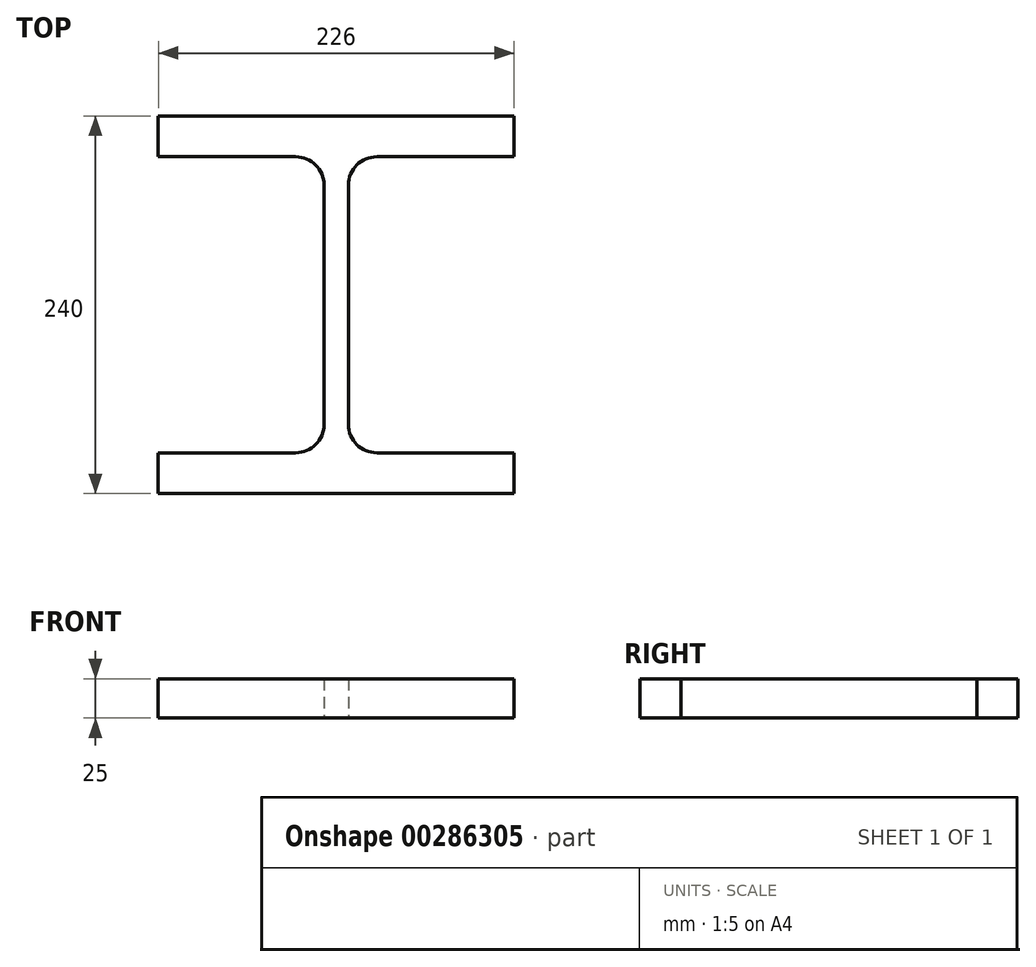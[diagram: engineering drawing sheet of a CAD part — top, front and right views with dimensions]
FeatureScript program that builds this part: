
annotation { "Feature Type Name" : "Feature", "Feature Type Description" : "" }
export const myFeature = defineFeature(function(context is Context, id is Id, definition is map)
    precondition{}
    {
        {
            var Q0;
            Q0=qCreatedBy(makeId("Top.planeOp"),FACE);
            var sketch = newSketch(context, id + "F0", { "sketchPlane" : qUnion([Q0])});
            skLineSegment(sketch, "E0", {"start": v(-45.16, 76.87) * mm, "end": v(180.84, 76.87) * mm});
            skLineSegment(sketch, "E1", {"start": v(-45.16, -163.13) * mm, "end": v(180.84, -163.13) * mm});
            skPoint(sketch, "E2.end.orphan", {"position": v(-45.16, -155.6) * mm});
            skLineSegment(sketch, "E3", {"start": v(-45.16, 76.87) * mm, "end": v(-45.16, 50.87) * mm});
            skLineSegment(sketch, "E4", {"start": v(-45.16, -163.13) * mm, "end": v(-45.16, -137.13) * mm});
            skLineSegment(sketch, "E5", {"start": v(180.84, -163.13) * mm, "end": v(180.84, -137.13) * mm});
            skLineSegment(sketch, "E6", {"start": v(180.84, 76.87) * mm, "end": v(180.84, 50.87) * mm});
            skLineSegment(sketch, "E7", {"start": v(180.84, 50.87) * mm, "end": v(93.59, 50.87) * mm});
            skLineSegment(sketch, "E8", {"start": v(60.09, -54.42) * mm, "end": v(60.09, -119.13) * mm});
            skLineSegment(sketch, "E9", {"start": v(60.09, 32.87) * mm, "end": v(60.09, -54.42) * mm});
            skLineSegment(sketch, "E10", {"start": v(75.59, -54.42) * mm, "end": v(75.59, 32.87) * mm});
            skLineSegment(sketch, "E11", {"start": v(75.59, -54.42) * mm, "end": v(75.59, -119.13) * mm});
            skLineSegment(sketch, "E12", {"start": v(-45.16, -137.13) * mm, "end": v(42.09, -137.13) * mm});
            skLineSegment(sketch, "E13", {"start": v(-45.16, 50.87) * mm, "end": v(42.09, 50.87) * mm});
            skPoint(sketch, "E14.end.orphan", {"position": v(67.84, -160.03) * mm});
            skPoint(sketch, "E15.orphan", {"position": v(54.84, 50.87) * mm});
            skPoint(sketch, "E16.visualSharp", {"position": v(60.09, 50.87) * mm});
            skArc(sketch, "E16.filletArc", {"start": v(60.09, 32.87) * mm, "mid": v(54.81, 45.6) * mm, "end": v(42.09, 50.87) * mm});
            skPoint(sketch, "E17.visualSharp", {"position": v(75.59, 50.87) * mm});
            skArc(sketch, "E17.filletArc", {"start": v(93.59, 50.87) * mm, "mid": v(80.86, 45.6) * mm, "end": v(75.59, 32.87) * mm});
            skPoint(sketch, "E18.orphan", {"position": v(75.59, -160.03) * mm});
            skPoint(sketch, "E19.orphan", {"position": v(60.09, -160.03) * mm});
            skLineSegment(sketch, "E20", {"start": v(93.59, -137.13) * mm, "end": v(180.84, -137.13) * mm});
            skPoint(sketch, "E21.visualSharp", {"position": v(60.09, -137.13) * mm});
            skArc(sketch, "E21.filletArc", {"start": v(42.09, -137.13) * mm, "mid": v(54.81, -131.86) * mm, "end": v(60.09, -119.13) * mm});
            skPoint(sketch, "E22.visualSharp", {"position": v(75.59, -137.13) * mm});
            skArc(sketch, "E22.filletArc", {"start": v(75.59, -119.13) * mm, "mid": v(80.86, -131.86) * mm, "end": v(93.59, -137.13) * mm});
            skPoint(sketch, "E23.start.orphan", {"position": v(180.84, -150.13) * mm});
            skSolve(sketch);
        }
        {
            var Q0;
            Q0=makeQuery(id+"F0.imprint","IMPRINT",FACE,{"disambiguationData":[TD([[makeQuery(id+"F0.imprint","IMPRINT",EDGE,{"derivedFrom":sQuery(id+"F0.wireOp",EDGE,"E0")}),-1.0]])]});
            extrude(context, id + "F1", {"entities" : qUnion([Q0]), "depth" : 25 * mm});
        }
    });
